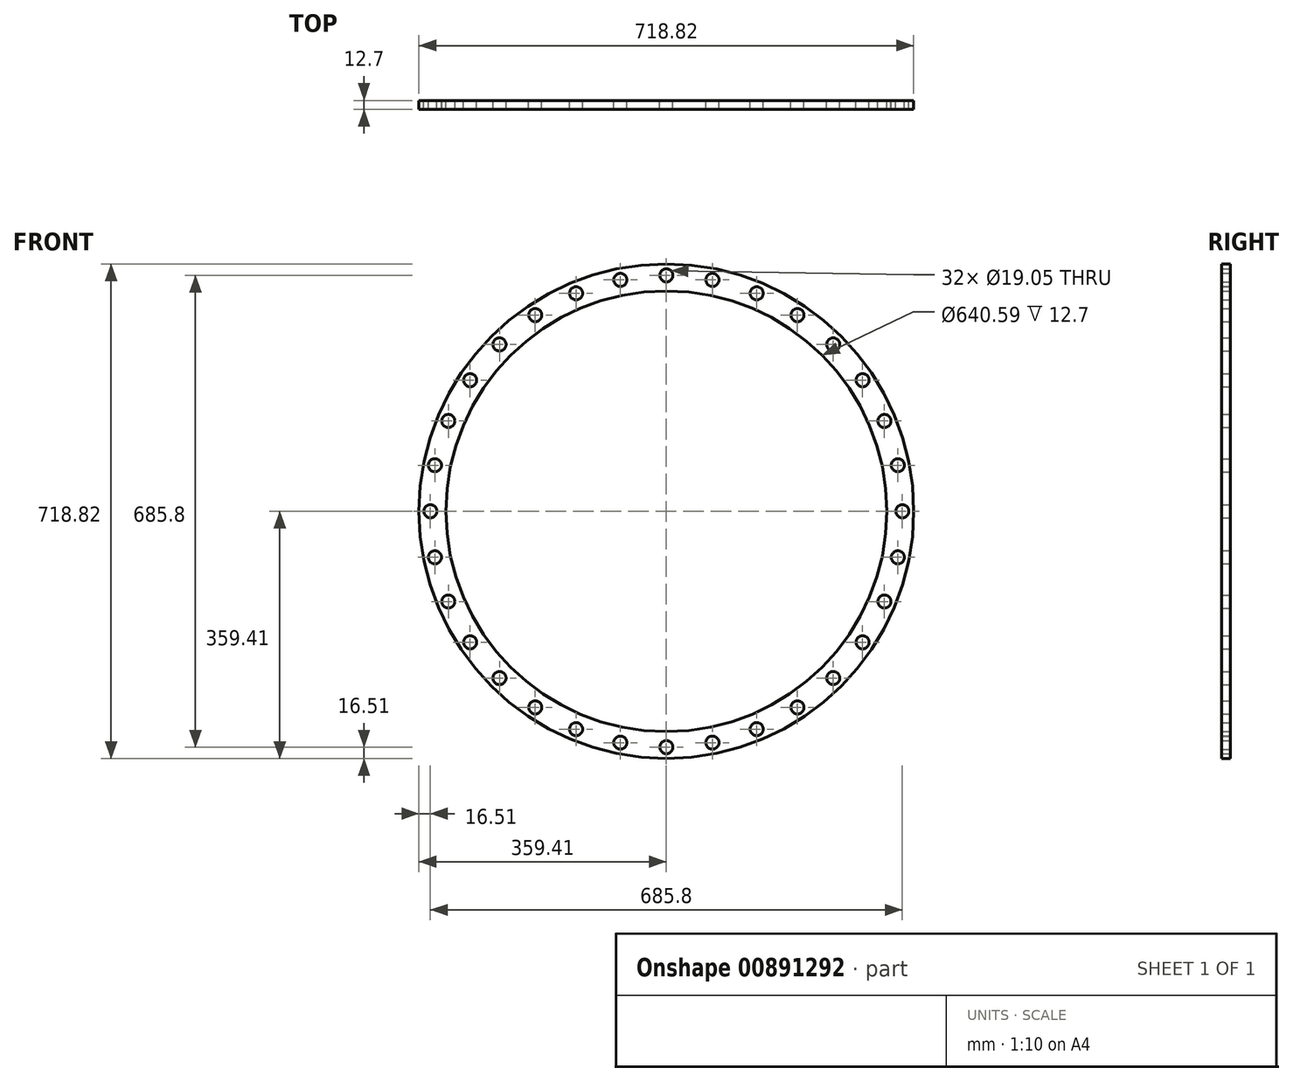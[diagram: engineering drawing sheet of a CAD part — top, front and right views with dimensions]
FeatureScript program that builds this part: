
annotation { "Feature Type Name" : "Feature", "Feature Type Description" : "" }
export const myFeature = defineFeature(function(context is Context, id is Id, definition is map)
    precondition{}
    {
        {
            var Q0;
            Q0=qCreatedBy(makeId("Front.planeOp"),FACE);
            var sketch = newSketch(context, id + "F0", { "sketchPlane" : qUnion([Q0])});
            skCircle(sketch, "E0", {"center": v(0, 0) * mm, "radius": 320.3 * mm});
            skCircle(sketch, "E1", {"center": v(0, 0) * mm, "radius": 359.41 * mm});
            skLineSegment(sketch, "E2", {"start": v(0, 0) * mm, "end": v(0, 359.41) * mm, "construction": true});
            skCircle(sketch, "E3", {"center": v(0, 0) * mm, "radius": 342.9 * mm, "construction": true});
            skCircle(sketch, "E4", {"center": v(0, 342.9) * mm, "radius": 9.53 * mm});
            skCircle(sketch, "E5.1.0", {"center": v(-66.9, 336.31) * mm, "radius": 9.53 * mm});
            skCircle(sketch, "E5.2.0", {"center": v(-131.22, 316.8) * mm, "radius": 9.52 * mm});
            skCircle(sketch, "E6.1.3.0", {"center": v(-190.5, 285.11) * mm, "radius": 9.53 * mm});
            skCircle(sketch, "E6.1.4.0", {"center": v(-242.47, 242.47) * mm, "radius": 9.53 * mm});
            skCircle(sketch, "E6.1.5.0", {"center": v(-285.11, 190.5) * mm, "radius": 9.53 * mm});
            skCircle(sketch, "E6.1.6.0", {"center": v(-316.8, 131.22) * mm, "radius": 9.53 * mm});
            skCircle(sketch, "E6.1.7.0", {"center": v(-336.31, 66.9) * mm, "radius": 9.53 * mm});
            skCircle(sketch, "E6.1.8.0", {"center": v(-342.9, 0) * mm, "radius": 9.53 * mm});
            skCircle(sketch, "E6.1.9.0", {"center": v(-336.31, -66.9) * mm, "radius": 9.53 * mm});
            skCircle(sketch, "E6.1.10.0", {"center": v(-316.8, -131.22) * mm, "radius": 9.53 * mm});
            skCircle(sketch, "E6.1.11.0", {"center": v(-285.11, -190.5) * mm, "radius": 9.53 * mm});
            skCircle(sketch, "E6.1.12.0", {"center": v(-242.47, -242.47) * mm, "radius": 9.53 * mm});
            skCircle(sketch, "E6.1.13.0", {"center": v(-190.5, -285.11) * mm, "radius": 9.53 * mm});
            skCircle(sketch, "E6.1.14.0", {"center": v(-131.22, -316.8) * mm, "radius": 9.53 * mm});
            skCircle(sketch, "E6.1.15.0", {"center": v(-66.9, -336.31) * mm, "radius": 9.53 * mm});
            skCircle(sketch, "E6.1.16.0", {"center": v(0, -342.9) * mm, "radius": 9.53 * mm});
            skCircle(sketch, "E6.1.17.0", {"center": v(66.9, -336.31) * mm, "radius": 9.53 * mm});
            skCircle(sketch, "E6.1.18.0", {"center": v(131.22, -316.8) * mm, "radius": 9.53 * mm});
            skCircle(sketch, "E6.1.19.0", {"center": v(190.5, -285.11) * mm, "radius": 9.53 * mm});
            skCircle(sketch, "E6.1.20.0", {"center": v(242.47, -242.47) * mm, "radius": 9.53 * mm});
            skCircle(sketch, "E6.1.21.0", {"center": v(285.11, -190.5) * mm, "radius": 9.53 * mm});
            skCircle(sketch, "E6.1.22.0", {"center": v(316.8, -131.22) * mm, "radius": 9.53 * mm});
            skCircle(sketch, "E6.1.23.0", {"center": v(336.31, -66.9) * mm, "radius": 9.53 * mm});
            skCircle(sketch, "E6.1.24.0", {"center": v(342.9, 0) * mm, "radius": 9.53 * mm});
            skCircle(sketch, "E6.1.25.0", {"center": v(336.31, 66.9) * mm, "radius": 9.53 * mm});
            skCircle(sketch, "E6.1.26.0", {"center": v(316.8, 131.22) * mm, "radius": 9.53 * mm});
            skCircle(sketch, "E6.1.27.0", {"center": v(285.11, 190.5) * mm, "radius": 9.53 * mm});
            skCircle(sketch, "E6.1.28.0", {"center": v(242.47, 242.47) * mm, "radius": 9.53 * mm});
            skCircle(sketch, "E6.1.29.0", {"center": v(190.5, 285.11) * mm, "radius": 9.53 * mm});
            skCircle(sketch, "E6.1.30.0", {"center": v(131.22, 316.8) * mm, "radius": 9.53 * mm});
            skCircle(sketch, "E6.1.31.0", {"center": v(66.9, 336.31) * mm, "radius": 9.53 * mm});
            skSolve(sketch);
        }
        {
            var Q0;
            Q0=makeQuery(id+"F0.imprint","IMPRINT",FACE,{"disambiguationData":[TD([[makeQuery(id+"F0.imprint","IMPRINT",EDGE,{"derivedFrom":sQuery(id+"F0.wireOp",EDGE,"E4")}),-1.0]])]});
            extrude(context, id + "F1", {"entities" : qUnion([Q0]), "depth" : 12.7 * mm, "offsetDistance" : 25.4 * mm});
        }
    });
